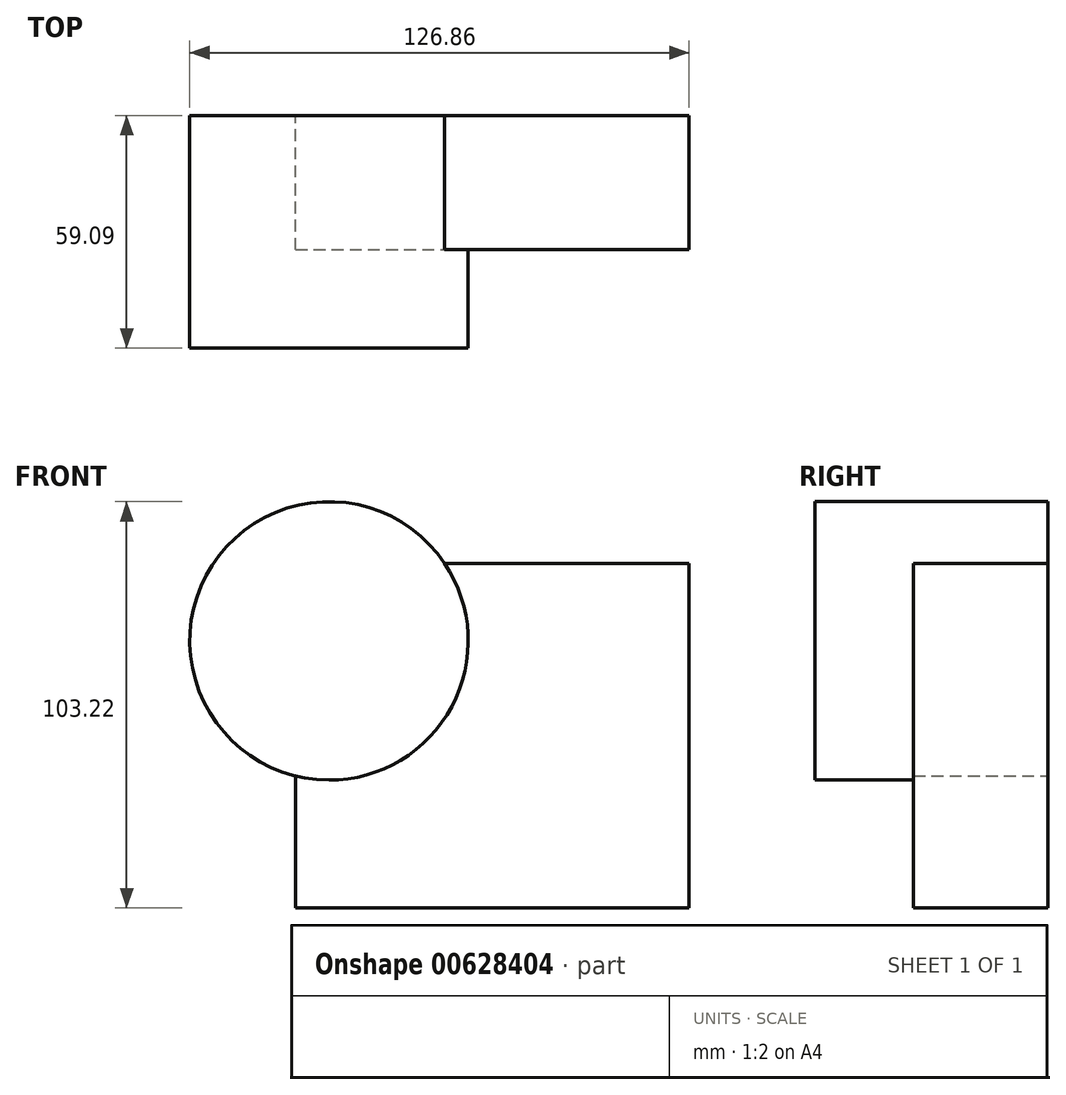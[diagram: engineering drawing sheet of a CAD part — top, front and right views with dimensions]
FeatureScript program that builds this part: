
annotation { "Feature Type Name" : "Feature", "Feature Type Description" : "" }
export const myFeature = defineFeature(function(context is Context, id is Id, definition is map)
    precondition{}
    {
        {
            var Q0;
            Q0=qCreatedBy(makeId("Front.planeOp"),FACE);
            var sketch = newSketch(context, id + "F0", { "sketchPlane" : qUnion([Q0])});
            skLineSegment(sketch, "E0.bottom", {"start": v(-42.94, 27.6) * mm, "end": v(57.05, 27.6) * mm});
            skLineSegment(sketch, "E0.top", {"start": v(-42.94, -59.96) * mm, "end": v(57.05, -59.96) * mm});
            skLineSegment(sketch, "E0.left", {"start": v(-42.94, 27.6) * mm, "end": v(-42.94, -59.96) * mm});
            skLineSegment(sketch, "E0.right", {"start": v(57.05, 27.6) * mm, "end": v(57.05, -59.96) * mm});
            skPoint(sketch, "E0.middle", {"position": v(7.05, -16.18) * mm});
            skSolve(sketch);
        }
        {
            var Q0;
            Q0 = qSketchRegion(id + "F0", true);
            extrude(context, id + "F1", {"entities" : qUnion([Q0]), "depth" : 34.07 * mm, "offsetDistance" : 25.4 * mm});
        }
        {
            var Q0;
            Q0=qCreatedBy(makeId("Front.planeOp"),FACE);
            var sketch = newSketch(context, id + "F2", { "sketchPlane" : qUnion([Q0])});
            skCircle(sketch, "E1", {"center": v(-34.44, 7.88) * mm, "radius": 35.38 * mm});
            skSolve(sketch);
        }
        {
            var Q0;
            Q0 = qSketchRegion(id + "F2", true);
            extrude(context, id + "F3", {"entities" : qUnion([Q0]), "operationType" : NewBodyOperationType.ADD, "depth" : 59.1 * mm, "offsetDistance" : 25.4 * mm});
        }
    });
